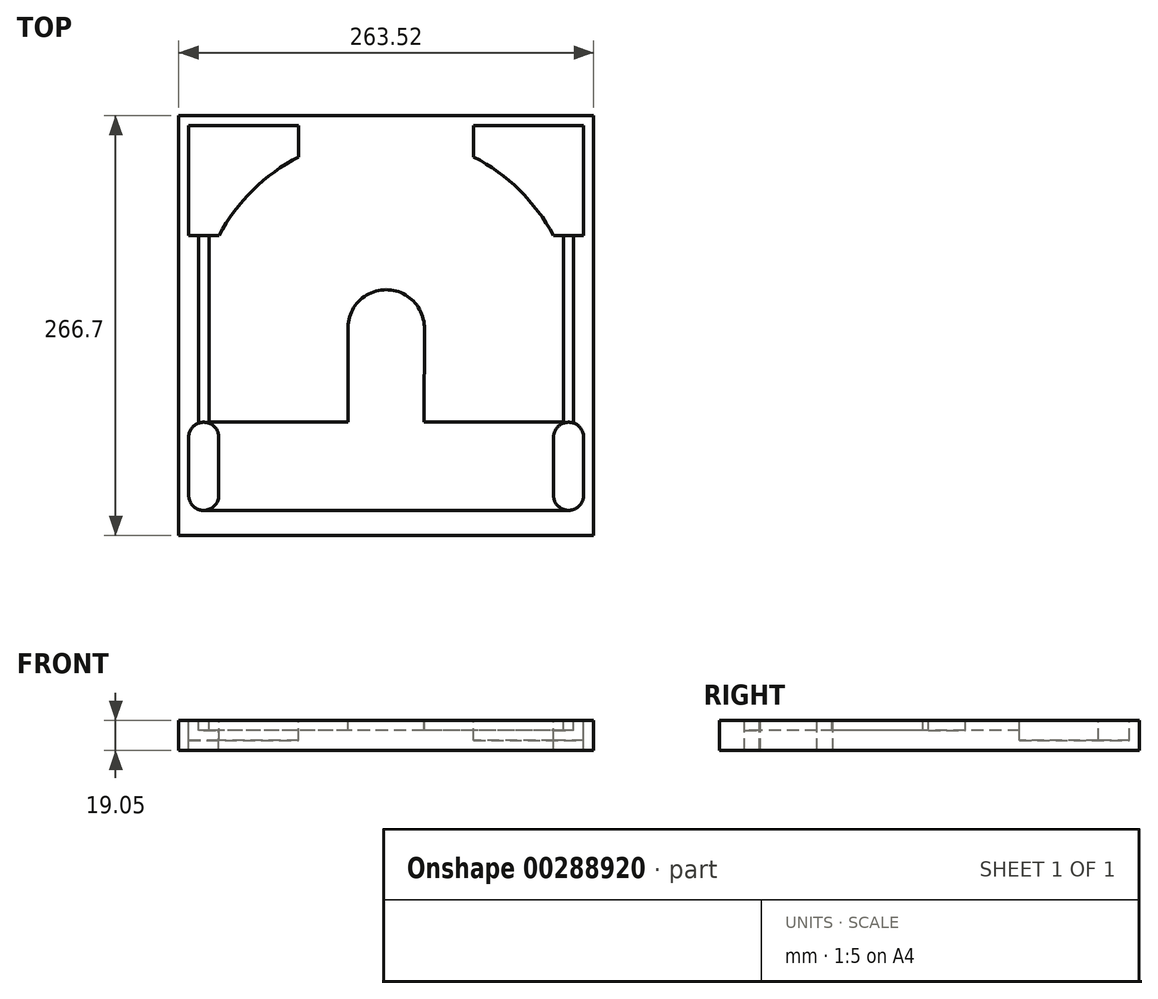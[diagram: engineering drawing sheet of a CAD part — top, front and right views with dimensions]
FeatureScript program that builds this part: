
annotation { "Feature Type Name" : "Feature", "Feature Type Description" : "" }
export const myFeature = defineFeature(function(context is Context, id is Id, definition is map)
    precondition{}
    {
        {
            var Q0;
            Q0=qCreatedBy(makeId("Top.planeOp"),FACE);
            var sketch = newSketch(context, id + "F0", { "sketchPlane" : qUnion([Q0])});
            skLineSegment(sketch, "E0.bottom", {"start": v(-134.94, 136.53) * mm, "end": v(134.94, 136.53) * mm});
            skLineSegment(sketch, "E0.top", {"start": v(-134.94, -136.53) * mm, "end": v(134.94, -136.53) * mm});
            skLineSegment(sketch, "E0.left", {"start": v(-134.94, 136.53) * mm, "end": v(-134.94, -136.53) * mm});
            skLineSegment(sketch, "E0.right", {"start": v(134.94, 136.53) * mm, "end": v(134.94, -136.53) * mm});
            skPoint(sketch, "E0.middle", {"position": v(0, 0) * mm});
            skSolve(sketch);
        }
        {
            var Q0;
            Q0 = qSketchRegion(id + "F0", true);
            extrude(context, id + "F1", {"entities" : qUnion([Q0]), "depth" : 19.05 * mm});
        }
        {
            var Q0;
            Q0=makeQuery(id+"F1.opExtrude","CAP_FACE",FACE,{"disambiguationData":[OSD([sQuery(id+"F0.wireOp",EDGE,"E0.bottom"),sQuery(id+"F0.wireOp",EDGE,"E0.top"),sQuery(id+"F0.wireOp",EDGE,"E0.left"),sQuery(id+"F0.wireOp",EDGE,"E0.right")])],"isStart":false});
            var sketch = newSketch(context, id + "F2", { "sketchPlane" : qUnion([Q0])});
            skLineSegment(sketch, "E1", {"start": v(-125.41, 136.53) * mm, "end": v(-125.41, -136.53) * mm, "construction": true});
            skLineSegment(sketch, "E2", {"start": v(125.41, 136.53) * mm, "end": v(125.41, -136.53) * mm, "construction": true});
            skLineSegment(sketch, "E3", {"start": v(-134.94, 127) * mm, "end": v(134.94, 127) * mm, "construction": true});
            skLineSegment(sketch, "E4", {"start": v(-134.94, -117.48) * mm, "end": v(134.94, -117.47) * mm, "construction": true});
            skArc(sketch, "E5", {"start": v(106.26, 57.15) * mm, "mid": v(84.68, 85.94) * mm, "end": v(55.56, 107.1) * mm});
            skLineSegment(sketch, "E6", {"start": v(-106.26, 57.15) * mm, "end": v(-125.41, 57.15) * mm});
            skLineSegment(sketch, "E7", {"start": v(-125.41, 57.15) * mm, "end": v(-125.41, 127) * mm});
            skLineSegment(sketch, "E8", {"start": v(-125.41, 127) * mm, "end": v(-55.56, 127) * mm});
            skLineSegment(sketch, "E9", {"start": v(-55.56, 127) * mm, "end": v(-55.56, 107.1) * mm});
            skLineSegment(sketch, "E10", {"start": v(55.56, 107.1) * mm, "end": v(55.56, 127) * mm});
            skLineSegment(sketch, "E11", {"start": v(55.56, 127) * mm, "end": v(125.41, 127) * mm});
            skLineSegment(sketch, "E12", {"start": v(125.41, 127) * mm, "end": v(125.41, 57.15) * mm});
            skLineSegment(sketch, "E13", {"start": v(125.41, 57.15) * mm, "end": v(106.26, 57.15) * mm});
            skArc(sketch, "E14.trimOffspring", {"start": v(-55.56, 107.1) * mm, "mid": v(-84.68, 85.94) * mm, "end": v(-106.26, 57.15) * mm});
            skSolve(sketch);
        }
        {
            var Q0;
            Q0 = qSketchRegion(id + "F2", true);
            extrude(context, id + "F3", {"entities" : qUnion([Q0]), "operationType" : NewBodyOperationType.REMOVE, "oppositeDirection" : true, "depth" : 12.7 * mm});
        }
        {
            var Q0;
            Q0=makeQuery(id+"F1.opExtrude","CAP_FACE",FACE,{"disambiguationData":[OSD([sQuery(id+"F0.wireOp",EDGE,"E0.bottom"),sQuery(id+"F0.wireOp",EDGE,"E0.top"),sQuery(id+"F0.wireOp",EDGE,"E0.left"),sQuery(id+"F0.wireOp",EDGE,"E0.right")])],"isStart":false});
            var sketch = newSketch(context, id + "F4", { "sketchPlane" : qUnion([Q0])});
            skLineSegment(sketch, "E15", {"start": v(-134.94, -117.48) * mm, "end": v(134.94, -117.48) * mm, "construction": true});
            skLineSegment(sketch, "E16", {"start": v(-125.41, 136.53) * mm, "end": v(-125.41, -136.53) * mm, "construction": true});
            skLineSegment(sketch, "E17", {"start": v(125.41, 136.53) * mm, "end": v(125.41, -136.53) * mm, "construction": true});
            skLineSegment(sketch, "E18", {"start": v(-134.94, -107.92) * mm, "end": v(-125.4, -107.92) * mm, "construction": true});
            skLineSegment(sketch, "E19", {"start": v(-134.94, -61.47) * mm, "end": v(134.94, -61.47) * mm, "construction": true});
            skLineSegment(sketch, "E20", {"start": v(-134.94, -107.96) * mm, "end": v(-125.4, -107.96) * mm, "construction": true});
            skLineSegment(sketch, "E21", {"start": v(-134.94, -71) * mm, "end": v(-125.41, -71) * mm, "construction": true});
            skLineSegment(sketch, "E22", {"start": v(-106.36, 136.53) * mm, "end": v(-106.36, -136.53) * mm, "construction": true});
            skLineSegment(sketch, "E23", {"start": v(106.36, 136.53) * mm, "end": v(106.36, -136.53) * mm, "construction": true});
            skLineSegment(sketch, "E24", {"start": v(-106.36, -71) * mm, "end": v(-106.36, -107.96) * mm});
            skLineSegment(sketch, "E25", {"start": v(-106.36, -107.96) * mm, "end": v(-106.38, -107.96) * mm});
            skLineSegment(sketch, "E26", {"start": v(-125.41, -107.96) * mm, "end": v(-125.41, -71) * mm});
            skLineSegment(sketch, "E27", {"start": v(106.36, -71) * mm, "end": v(106.36, -107.92) * mm});
            skLineSegment(sketch, "E28", {"start": v(125.41, -107.92) * mm, "end": v(125.41, -71) * mm});
            skArc(sketch, "E29", {"start": v(125.41, -71.5) * mm, "mid": v(115.89, -61.47) * mm, "end": v(106.36, -71.5) * mm});
            skArc(sketch, "E30", {"start": v(106.36, -107.23) * mm, "mid": v(115.89, -117.48) * mm, "end": v(125.41, -107.23) * mm});
            skArc(sketch, "E31", {"start": v(-106.36, -71.5) * mm, "mid": v(-115.89, -61.47) * mm, "end": v(-125.41, -71.5) * mm});
            skArc(sketch, "E32", {"start": v(-125.4, -107.92) * mm, "mid": v(-115.89, -117.48) * mm, "end": v(-106.38, -107.92) * mm});
            skLineSegment(sketch, "E33.trimOffspring", {"start": v(125.41, -71) * mm, "end": v(134.94, -71) * mm, "construction": true});
            skLineSegment(sketch, "E34.trimOffspring", {"start": v(125.41, -107.96) * mm, "end": v(134.94, -107.96) * mm, "construction": true});
            skLineSegment(sketch, "E35.trimOffspring", {"start": v(125.41, -107.92) * mm, "end": v(134.94, -107.92) * mm, "construction": true});
            skLineSegment(sketch, "E36.trimOffspring", {"start": v(-106.36, -71) * mm, "end": v(106.36, -71) * mm, "construction": true});
            skLineSegment(sketch, "E37.trimOffspring", {"start": v(-106.38, -107.96) * mm, "end": v(106.36, -107.96) * mm, "construction": true});
            skLineSegment(sketch, "E38.trimOffspring", {"start": v(-106.38, -107.92) * mm, "end": v(106.36, -107.92) * mm, "construction": true});
            skLineSegment(sketch, "E39.trimOffspring", {"start": v(-125.4, -107.96) * mm, "end": v(-125.41, -107.96) * mm});
            skLineSegment(sketch, "E40", {"start": v(-134.94, -90.06) * mm, "end": v(134.94, -90.06) * mm, "construction": true});
            skLineSegment(sketch, "E41", {"start": v(-115.89, -90.06) * mm, "end": v(-115.89, 57.15) * mm, "construction": true});
            skLineSegment(sketch, "E42", {"start": v(115.89, -71) * mm, "end": v(115.89, -107.92) * mm, "construction": true});
            skSolve(sketch);
        }
        {
            var Q0;
            Q0 = qSketchRegion(id + "F4", true);
            extrude(context, id + "F5", {"entities" : qUnion([Q0]), "operationType" : NewBodyOperationType.REMOVE, "endBound" : BoundingType.UP_TO_NEXT, "oppositeDirection" : true, "depth" : 25.4 * mm});
        }
        {
            var Q0;
            Q0=makeQuery(id+"F1.opExtrude","CAP_FACE",FACE,{"disambiguationData":[OSD([sQuery(id+"F0.wireOp",EDGE,"E0.bottom"),sQuery(id+"F0.wireOp",EDGE,"E0.top"),sQuery(id+"F0.wireOp",EDGE,"E0.left"),sQuery(id+"F0.wireOp",EDGE,"E0.right")])],"isStart":false});
            var sketch = newSketch(context, id + "F6", { "sketchPlane" : qUnion([Q0])});
            skLineSegment(sketch, "E43.bottom", {"start": v(-134.94, 136.53) * mm, "end": v(-131.76, 136.53) * mm});
            skLineSegment(sketch, "E43.top", {"start": v(-134.94, -136.53) * mm, "end": v(-131.76, -136.53) * mm});
            skLineSegment(sketch, "E43.left", {"start": v(-134.94, 136.53) * mm, "end": v(-134.94, -136.53) * mm});
            skLineSegment(sketch, "E43.right", {"start": v(-131.76, 136.53) * mm, "end": v(-131.76, -136.53) * mm});
            skLineSegment(sketch, "E44.bottom", {"start": v(134.94, 136.53) * mm, "end": v(131.76, 136.53) * mm});
            skLineSegment(sketch, "E44.top", {"start": v(134.94, -136.53) * mm, "end": v(131.76, -136.53) * mm});
            skLineSegment(sketch, "E44.left", {"start": v(134.94, 136.53) * mm, "end": v(134.94, -136.53) * mm});
            skLineSegment(sketch, "E44.right", {"start": v(131.76, 136.53) * mm, "end": v(131.76, -136.53) * mm});
            skSolve(sketch);
        }
        {
            var Q0;
            Q0 = qSketchRegion(id + "F6", true);
            extrude(context, id + "F7", {"entities" : qUnion([Q0]), "operationType" : NewBodyOperationType.REMOVE, "endBound" : BoundingType.UP_TO_NEXT, "oppositeDirection" : true, "depth" : 25.4 * mm});
        }
        {
            var Q0;
            Q0=makeQuery(id+"F1.opExtrude","CAP_FACE",FACE,{"disambiguationData":[OSD([sQuery(id+"F0.wireOp",EDGE,"E0.bottom"),sQuery(id+"F0.wireOp",EDGE,"E0.top"),sQuery(id+"F0.wireOp",EDGE,"E0.left"),sQuery(id+"F0.wireOp",EDGE,"E0.right")])],"isStart":false});
            var sketch = newSketch(context, id + "F8", { "sketchPlane" : qUnion([Q0])});
            skLineSegment(sketch, "E45.bottom", {"start": v(-131.76, 136.53) * mm, "end": v(131.76, 136.53) * mm});
            skLineSegment(sketch, "E45.top", {"start": v(-131.76, 133.35) * mm, "end": v(131.76, 133.35) * mm});
            skLineSegment(sketch, "E45.left", {"start": v(-131.76, 136.53) * mm, "end": v(-131.76, 133.35) * mm});
            skLineSegment(sketch, "E45.right", {"start": v(131.76, 136.53) * mm, "end": v(131.76, 133.35) * mm});
            skSolve(sketch);
        }
        {
            var Q0;
            Q0 = qSketchRegion(id + "F8", true);
            extrude(context, id + "F9", {"entities" : qUnion([Q0]), "operationType" : NewBodyOperationType.REMOVE, "endBound" : BoundingType.UP_TO_NEXT, "oppositeDirection" : true, "depth" : 25.4 * mm});
        }
        {
            var Q0;
            Q0=makeQuery(id+"F1.opExtrude","CAP_FACE",FACE,{"disambiguationData":[OSD([sQuery(id+"F0.wireOp",EDGE,"E0.bottom"),sQuery(id+"F0.wireOp",EDGE,"E0.top"),sQuery(id+"F0.wireOp",EDGE,"E0.left"),sQuery(id+"F0.wireOp",EDGE,"E0.right")])],"isStart":false});
            var sketch = newSketch(context, id + "F10", { "sketchPlane" : qUnion([Q0])});
            skLineSegment(sketch, "E46", {"start": v(0, -136.53) * mm, "end": v(0, 133.35) * mm, "construction": true});
            skLineSegment(sketch, "E47", {"start": v(24.25, -0.65) * mm, "end": v(24.13, -0.65) * mm, "construction": true});
            skPoint(sketch, "E47.startSnap0", {"position": v(131.76, -1.59) * mm});
            skLineSegment(sketch, "E48", {"start": v(131.76, -136.53) * mm, "end": v(-131.76, 133.35) * mm, "construction": true});
            skArc(sketch, "E49", {"start": v(0, 7.3) * mm, "mid": v(-0.05, 7.3) * mm, "end": v(-0.1, 7.3) * mm});
            skLineSegment(sketch, "E50", {"start": v(24.13, -136.53) * mm, "end": v(24.13, 133.35) * mm, "construction": true});
            skLineSegment(sketch, "E51", {"start": v(-24.13, -136.53) * mm, "end": v(-24.13, 133.35) * mm, "construction": true});
            skLineSegment(sketch, "E52", {"start": v(131.76, 20.54) * mm, "end": v(-131.76, 20.54) * mm, "construction": true});
            skLineSegment(sketch, "E53", {"start": v(0, -10.48) * mm, "end": v(131.76, -10.48) * mm, "construction": true});
            skLineSegment(sketch, "E54", {"start": v(0, -10.48) * mm, "end": v(-131.76, -10.48) * mm, "construction": true});
            skLineSegment(sketch, "E55", {"start": v(0, 7.3) * mm, "end": v(131.76, 7.3) * mm, "construction": true});
            skLineSegment(sketch, "E56", {"start": v(0, 7.3) * mm, "end": v(-131.76, 6.5) * mm, "construction": true});
            skLineSegment(sketch, "E57", {"start": v(131.76, -29.95) * mm, "end": v(-131.76, -29.95) * mm, "construction": true});
            skLineSegment(sketch, "E58", {"start": v(131.76, -53.64) * mm, "end": v(-131.76, -53.64) * mm, "construction": true});
            skArc(sketch, "E59", {"start": v(24.13, -4.2) * mm, "mid": v(0, 22.68) * mm, "end": v(-24.13, -4.2) * mm});
            skLineSegment(sketch, "E60", {"start": v(115.89, -61.47) * mm, "end": v(24.13, -61.47) * mm});
            skPoint(sketch, "E60.startSnap0", {"position": v(115.89, -61.47) * mm});
            skLineSegment(sketch, "E61", {"start": v(115.89, -117.48) * mm, "end": v(-115.89, -117.48) * mm});
            skPoint(sketch, "E62.orphan", {"position": v(131.76, 0) * mm});
            skLineSegment(sketch, "E63.trimOffspring", {"start": v(0.78, -0.79) * mm, "end": v(-0.77, -0.8) * mm, "construction": true});
            skLineSegment(sketch, "E64.trimOffspring", {"start": v(-24.13, -0.94) * mm, "end": v(-24.26, -0.94) * mm, "construction": true});
            skPoint(sketch, "E65.orphan", {"position": v(-131.76, -1.59) * mm});
            skLineSegment(sketch, "E66", {"start": v(24.25, -0.65) * mm, "end": v(24.13, -61.47) * mm});
            skLineSegment(sketch, "E67", {"start": v(-24.13, -0.94) * mm, "end": v(-24.13, -61.47) * mm});
            skLineSegment(sketch, "E68.trimOffspring", {"start": v(-24.13, -61.47) * mm, "end": v(-115.89, -61.47) * mm});
            skArc(sketch, "E69", {"start": v(-106.36, -71.5) * mm, "mid": v(-108.97, -64.44) * mm, "end": v(-115.89, -61.47) * mm});
            skArc(sketch, "E70", {"start": v(-115.89, -117.48) * mm, "mid": v(-115.88, -117.48) * mm, "end": v(-115.87, -117.48) * mm});
            skLineSegment(sketch, "E71", {"start": v(-106.36, -107.96) * mm, "end": v(-106.36, -71.5) * mm});
            skArc(sketch, "E72", {"start": v(106.36, -107.23) * mm, "mid": v(108.9, -114.43) * mm, "end": v(115.89, -117.48) * mm});
            skArc(sketch, "E73", {"start": v(115.89, -61.47) * mm, "mid": v(108.97, -64.44) * mm, "end": v(106.36, -71.5) * mm});
            skLineSegment(sketch, "E74", {"start": v(106.36, -71.5) * mm, "end": v(106.36, -107.23) * mm});
            skLineSegment(sketch, "E75.trimOffspring", {"start": v(-58.47, -61.47) * mm, "end": v(131.76, 133.35) * mm, "construction": true});
            skSolve(sketch);
        }
        {
            var Q0;
            {var subQ6=sQuery(id+"F10.wireOp",EDGE,"E60");Q0=makeQuery(id+"F10.imprint","IMPRINT",FACE,{"disambiguationData":[TD([[makeQuery(id+"F10.imprint","IMPRINT",EDGE,{"derivedFrom":subQ6}),1.0]])]});}
            extrude(context, id + "F11", {"entities" : qUnion([Q0]), "operationType" : NewBodyOperationType.REMOVE, "oppositeDirection" : true, "depth" : 6.35 * mm});
        }
        {
            var Q0;
            Q0=makeQuery(id+"F1.opExtrude","CAP_FACE",FACE,{"disambiguationData":[OSD([sQuery(id+"F0.wireOp",EDGE,"E0.bottom"),sQuery(id+"F0.wireOp",EDGE,"E0.top"),sQuery(id+"F0.wireOp",EDGE,"E0.left"),sQuery(id+"F0.wireOp",EDGE,"E0.right")])],"isStart":false});
            var sketch = newSketch(context, id + "F12", { "sketchPlane" : qUnion([Q0])});
            skLineSegment(sketch, "E76", {"start": v(-115.83, 57.15) * mm, "end": v(-115.83, -136.53) * mm, "construction": true});
            skLineSegment(sketch, "E77", {"start": v(115.83, 57.15) * mm, "end": v(115.89, -136.52) * mm, "construction": true});
            skLineSegment(sketch, "E78", {"start": v(-119.07, 57.15) * mm, "end": v(-119.07, -61.47) * mm, "construction": true});
            skLineSegment(sketch, "E79", {"start": v(-112.6, 57.15) * mm, "end": v(-112.6, -136.53) * mm, "construction": true});
            skLineSegment(sketch, "E80", {"start": v(112.6, 57.15) * mm, "end": v(112.6, -61.47) * mm, "construction": true});
            skLineSegment(sketch, "E81", {"start": v(119.07, 57.15) * mm, "end": v(119.07, -136.53) * mm, "construction": true});
            skLineSegment(sketch, "E82", {"start": v(112.6, 57.15) * mm, "end": v(112.6, -61.47) * mm});
            skLineSegment(sketch, "E83", {"start": v(119.07, -62.02) * mm, "end": v(119.07, 57.15) * mm});
            skLineSegment(sketch, "E84", {"start": v(-112.6, -61.47) * mm, "end": v(-112.6, 57.15) * mm});
            skLineSegment(sketch, "E85", {"start": v(-119.07, 57.15) * mm, "end": v(-119.07, -61.47) * mm});
            skLineSegment(sketch, "E86", {"start": v(-115.89, -61.47) * mm, "end": v(-115.83, -61.47) * mm});
            skLineSegment(sketch, "E87", {"start": v(115.89, -61.47) * mm, "end": v(112.6, -61.47) * mm});
            skLineSegment(sketch, "E88", {"start": v(-112.6, -61.47) * mm, "end": v(-115.89, -61.47) * mm});
            skLineSegment(sketch, "E89.trimOffspring", {"start": v(-119.07, -62.02) * mm, "end": v(-119.07, -136.53) * mm, "construction": true});
            skLineSegment(sketch, "E90", {"start": v(112.6, 57.15) * mm, "end": v(119.07, 57.15) * mm});
            skArc(sketch, "E91", {"start": v(119.07, -62.02) * mm, "mid": v(117.5, -61.6) * mm, "end": v(115.89, -61.47) * mm});
            skLineSegment(sketch, "E92", {"start": v(-119.07, -62.02) * mm, "end": v(-119.07, -61.47) * mm});
            skArc(sketch, "E93", {"start": v(-115.83, -61.47) * mm, "mid": v(-117.48, -61.6) * mm, "end": v(-119.07, -62.02) * mm});
            skLineSegment(sketch, "E94", {"start": v(-119.07, 57.15) * mm, "end": v(-112.6, 57.15) * mm});
            skSolve(sketch);
        }
        {
            var Q0;
            Q0 = qSketchRegion(id + "F12", true);
            extrude(context, id + "F13", {"entities" : qUnion([Q0]), "operationType" : NewBodyOperationType.REMOVE, "oppositeDirection" : true, "depth" : 6.35 * mm});
        }
        {
            var Q0;
            Q0=makeQuery(id+"F1.opExtrude","CAP_FACE",FACE,{"disambiguationData":[OSD([sQuery(id+"F0.wireOp",EDGE,"E0.bottom"),sQuery(id+"F0.wireOp",EDGE,"E0.top"),sQuery(id+"F0.wireOp",EDGE,"E0.left"),sQuery(id+"F0.wireOp",EDGE,"E0.right")])],"isStart":false});
            var sketch = newSketch(context, id + "F14", { "sketchPlane" : qUnion([Q0])});
            skLineSegment(sketch, "E95", {"start": v(-131.76, -136.53) * mm, "end": v(131.76, -136.53) * mm});
            skLineSegment(sketch, "E96", {"start": v(131.76, -136.53) * mm, "end": v(131.76, -133.35) * mm});
            skLineSegment(sketch, "E97", {"start": v(131.76, -133.35) * mm, "end": v(-131.76, -133.35) * mm});
            skLineSegment(sketch, "E98", {"start": v(-131.76, -133.35) * mm, "end": v(-131.76, -136.53) * mm});
            skSolve(sketch);
        }
        {
            var Q0;
            Q0 = qSketchRegion(id + "F14", true);
            extrude(context, id + "F15", {"entities" : qUnion([Q0]), "operationType" : NewBodyOperationType.REMOVE, "endBound" : BoundingType.UP_TO_NEXT, "oppositeDirection" : true, "depth" : 25.4 * mm});
        }
    });
